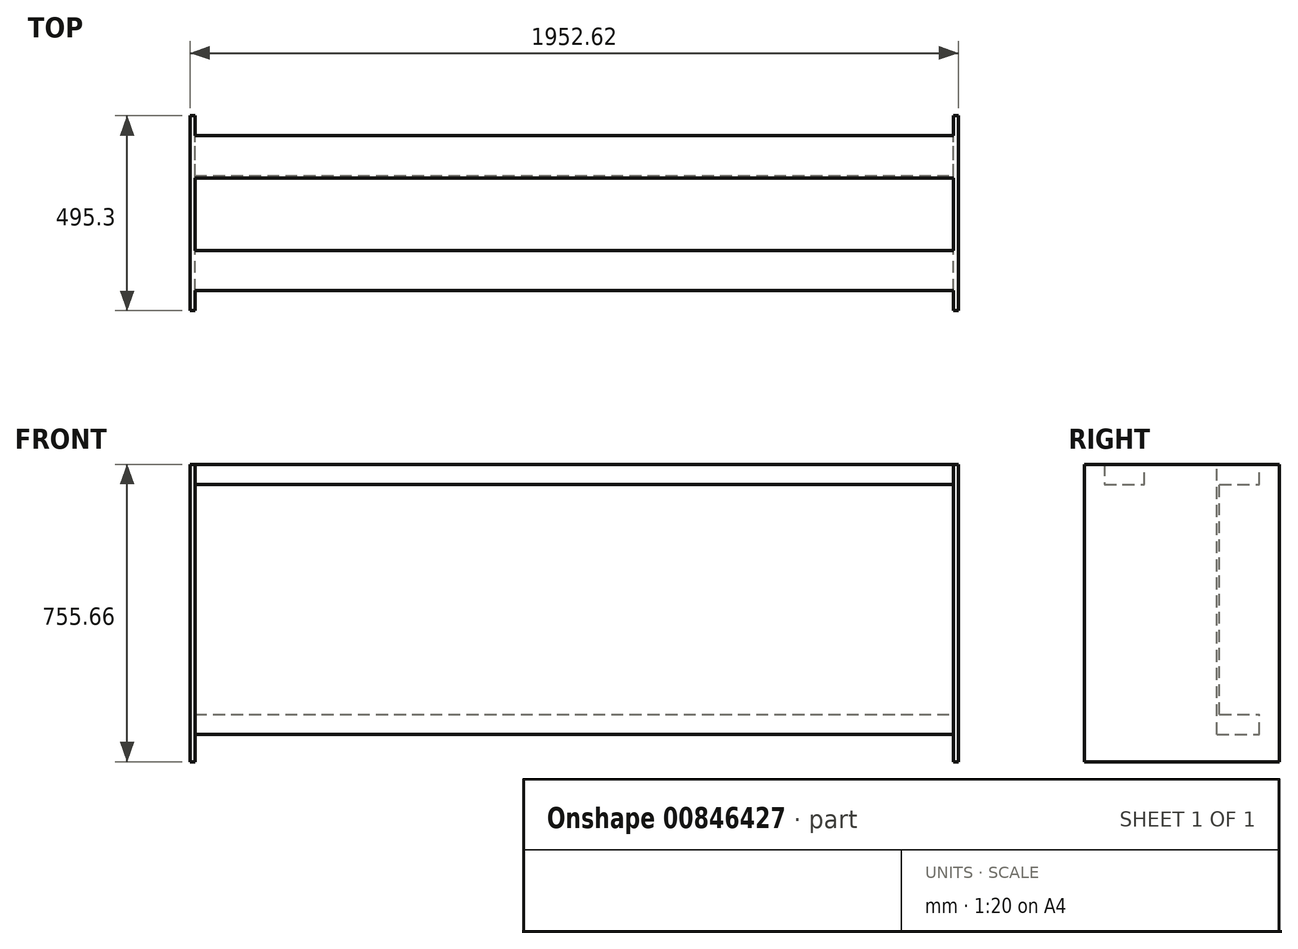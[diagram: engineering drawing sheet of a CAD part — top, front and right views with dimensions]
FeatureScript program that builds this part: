
annotation { "Feature Type Name" : "Feature", "Feature Type Description" : "" }
export const myFeature = defineFeature(function(context is Context, id is Id, definition is map)
    precondition{}
    {
        {
            var Q0;
            Q0=qCreatedBy(makeId("Front.planeOp"),FACE);
            var sketch = newSketch(context, id + "F0", { "sketchPlane" : qUnion([Q0])});
            skLineSegment(sketch, "E0.bottom", {"start": v(-976.31, -377.83) * mm, "end": v(976.31, -377.83) * mm});
            skLineSegment(sketch, "E0.top", {"start": v(-976.31, 377.83) * mm, "end": v(976.31, 377.83) * mm});
            skLineSegment(sketch, "E0.left", {"start": v(-976.31, -377.83) * mm, "end": v(-976.31, 377.83) * mm});
            skLineSegment(sketch, "E0.right", {"start": v(976.31, -377.83) * mm, "end": v(976.31, 377.83) * mm});
            skPoint(sketch, "E0.middle", {"position": v(0, 0) * mm});
            skLineSegment(sketch, "E1.0", {"start": v(-963.61, -377.83) * mm, "end": v(-963.61, 377.83) * mm});
            skLineSegment(sketch, "E2.0", {"start": v(963.61, -377.83) * mm, "end": v(963.61, 377.83) * mm});
            skLineSegment(sketch, "E3.0", {"start": v(-976.31, 327.03) * mm, "end": v(976.31, 327.03) * mm});
            skLineSegment(sketch, "E4.0", {"start": v(-976.31, -307.98) * mm, "end": v(976.31, -307.98) * mm});
            skLineSegment(sketch, "E5.0", {"start": v(-976.31, -257.18) * mm, "end": v(976.31, -257.18) * mm});
            skSolve(sketch);
        }
        {
            var Q0;
            {var subQ0=sQuery(id+"F0.wireOp",EDGE,"E0.left");var subQ1=sQuery(id+"F0.wireOp",EDGE,"E0.bottom");var subQ2=makeQuery(id+"F0.imprint","INTERSECT",VERTEX,{"derivedFrom":[subQ1,subQ0]});Q0=makeQuery(id+"F0.imprint","IMPRINT",FACE,{"disambiguationData":[TD([[makeQuery(id+"F0.imprint","IMPRINT",EDGE,{"disambiguationData":[TD([[subQ2,-1.0]])],"derivedFrom":subQ1}),1.0]])]});}
            var Q1;
            {var subQ0=sQuery(id+"F0.wireOp",EDGE,"E4.0");var subQ1=sQuery(id+"F0.wireOp",EDGE,"E0.left");var subQ2=makeQuery(id+"F0.imprint","INTERSECT",VERTEX,{"derivedFrom":[subQ1,subQ0]});Q1=makeQuery(id+"F0.imprint","IMPRINT",FACE,{"disambiguationData":[TD([[makeQuery(id+"F0.imprint","IMPRINT",EDGE,{"disambiguationData":[TD([[subQ2,-1.0]])],"derivedFrom":subQ1}),-1.0]])]});}
            var Q2;
            {var subQ0=sQuery(id+"F0.wireOp",EDGE,"E3.0");var subQ1=sQuery(id+"F0.wireOp",EDGE,"E0.left");var subQ2=makeQuery(id+"F0.imprint","INTERSECT",VERTEX,{"derivedFrom":[subQ1,subQ0]});Q2=makeQuery(id+"F0.imprint","IMPRINT",FACE,{"disambiguationData":[TD([[makeQuery(id+"F0.imprint","IMPRINT",EDGE,{"disambiguationData":[TD([[subQ2,1.0]])],"derivedFrom":subQ1}),-1.0]])]});}
            var Q3;
            {var subQ0=sQuery(id+"F0.wireOp",EDGE,"E0.left");var subQ1=sQuery(id+"F0.wireOp",EDGE,"E0.top");var subQ2=makeQuery(id+"F0.imprint","INTERSECT",VERTEX,{"derivedFrom":[subQ1,subQ0]});Q3=makeQuery(id+"F0.imprint","IMPRINT",FACE,{"disambiguationData":[TD([[makeQuery(id+"F0.imprint","IMPRINT",EDGE,{"disambiguationData":[TD([[subQ2,-1.0]])],"derivedFrom":subQ1}),-1.0]])]});}
            extrude(context, id + "F1", {"entities" : qUnion([Q0, Q1, Q2, Q3]), "depth" : 495.3 * mm, "offsetDistance" : 25.4 * mm});
        }
        {
            var Q0;
            {var subQ0=sQuery(id+"F0.wireOp",EDGE,"E1.0");var subQ1=sQuery(id+"F0.wireOp",EDGE,"E0.top");var subQ2=makeQuery(id+"F0.imprint","INTERSECT",VERTEX,{"derivedFrom":[subQ1,subQ0]});Q0=makeQuery(id+"F0.imprint","IMPRINT",FACE,{"disambiguationData":[TD([[makeQuery(id+"F0.imprint","IMPRINT",EDGE,{"disambiguationData":[TD([[subQ2,-1.0]])],"derivedFrom":subQ1}),-1.0]])]});}
            var Q1;
            {var subQ0=sQuery(id+"F0.wireOp",EDGE,"E4.0");var subQ1=sQuery(id+"F0.wireOp",EDGE,"E1.0");var subQ2=makeQuery(id+"F0.imprint","INTERSECT",VERTEX,{"derivedFrom":[subQ1,subQ0]});Q1=makeQuery(id+"F0.imprint","IMPRINT",FACE,{"disambiguationData":[TD([[makeQuery(id+"F0.imprint","IMPRINT",EDGE,{"disambiguationData":[TD([[subQ2,-1.0]])],"derivedFrom":subQ1}),-1.0]])]});}
            extrude(context, id + "F2", {"entities" : qUnion([Q0, Q1]), "operationType" : NewBodyOperationType.ADD, "depth" : 152.4 * mm, "offsetDistance" : 25.4 * mm});
        }
        {
            var Q0;
            {var subQ0=sQuery(id+"F0.wireOp",EDGE,"E5.0");var subQ1=sQuery(id+"F0.wireOp",EDGE,"E1.0");var subQ2=makeQuery(id+"F0.imprint","INTERSECT",VERTEX,{"derivedFrom":[subQ1,subQ0]});Q0=makeQuery(id+"F0.imprint","IMPRINT",FACE,{"disambiguationData":[TD([[makeQuery(id+"F0.imprint","IMPRINT",EDGE,{"disambiguationData":[TD([[subQ2,-1.0]])],"derivedFrom":subQ1}),-1.0]])]});}
            var Q1;
            {var subQ0=sQuery(id+"F0.wireOp",EDGE,"E1.0");var subQ1=sQuery(id+"F0.wireOp",EDGE,"E0.top");var subQ2=makeQuery(id+"F0.imprint","INTERSECT",VERTEX,{"derivedFrom":[subQ1,subQ0]});Q1=makeQuery(id+"F0.imprint","IMPRINT",FACE,{"disambiguationData":[TD([[makeQuery(id+"F0.imprint","IMPRINT",EDGE,{"disambiguationData":[TD([[subQ2,-1.0]])],"derivedFrom":subQ1}),-1.0]])]});}
            var Q2;
            {var subQ0=sQuery(id+"F0.wireOp",EDGE,"E4.0");var subQ1=sQuery(id+"F0.wireOp",EDGE,"E1.0");var subQ2=makeQuery(id+"F0.imprint","INTERSECT",VERTEX,{"derivedFrom":[subQ1,subQ0]});Q2=makeQuery(id+"F0.imprint","IMPRINT",FACE,{"disambiguationData":[TD([[makeQuery(id+"F0.imprint","IMPRINT",EDGE,{"disambiguationData":[TD([[subQ2,-1.0]])],"derivedFrom":subQ1}),-1.0]])]});}
            extrude(context, id + "F3", {"entities" : qUnion([Q0, Q1, Q2]), "operationType" : NewBodyOperationType.ADD, "depth" : 158.75 * mm, "offsetDistance" : 25.4 * mm});
        }
        {
            var Q0;
            {var subQ0=sQuery(id+"F0.wireOp",EDGE,"E3.0");var subQ1=sQuery(id+"F0.wireOp",EDGE,"E0.right");var subQ2=makeQuery(id+"F0.imprint","INTERSECT",VERTEX,{"derivedFrom":[subQ1,subQ0]});Q0=makeQuery(id+"F0.imprint","IMPRINT",FACE,{"disambiguationData":[TD([[makeQuery(id+"F0.imprint","IMPRINT",EDGE,{"disambiguationData":[TD([[subQ2,1.0]])],"derivedFrom":subQ1}),1.0]])]});}
            var Q1;
            {var subQ0=sQuery(id+"F0.wireOp",EDGE,"E0.right");var subQ1=sQuery(id+"F0.wireOp",EDGE,"E0.top");var subQ2=makeQuery(id+"F0.imprint","INTERSECT",VERTEX,{"derivedFrom":[subQ1,subQ0]});Q1=makeQuery(id+"F0.imprint","IMPRINT",FACE,{"disambiguationData":[TD([[makeQuery(id+"F0.imprint","IMPRINT",EDGE,{"disambiguationData":[TD([[subQ2,1.0]])],"derivedFrom":subQ1}),-1.0]])]});}
            var Q2;
            {var subQ0=sQuery(id+"F0.wireOp",EDGE,"E4.0");var subQ1=sQuery(id+"F0.wireOp",EDGE,"E0.right");var subQ2=makeQuery(id+"F0.imprint","INTERSECT",VERTEX,{"derivedFrom":[subQ1,subQ0]});Q2=makeQuery(id+"F0.imprint","IMPRINT",FACE,{"disambiguationData":[TD([[makeQuery(id+"F0.imprint","IMPRINT",EDGE,{"disambiguationData":[TD([[subQ2,-1.0]])],"derivedFrom":subQ1}),1.0]])]});}
            var Q3;
            {var subQ0=sQuery(id+"F0.wireOp",EDGE,"E0.right");var subQ1=sQuery(id+"F0.wireOp",EDGE,"E0.bottom");var subQ2=makeQuery(id+"F0.imprint","INTERSECT",VERTEX,{"derivedFrom":[subQ1,subQ0]});Q3=makeQuery(id+"F0.imprint","IMPRINT",FACE,{"disambiguationData":[TD([[makeQuery(id+"F0.imprint","IMPRINT",EDGE,{"disambiguationData":[TD([[subQ2,1.0]])],"derivedFrom":subQ1}),1.0]])]});}
            extrude(context, id + "F4", {"entities" : qUnion([Q0, Q1, Q2, Q3]), "operationType" : NewBodyOperationType.ADD, "depth" : 495.3 * mm, "offsetDistance" : 25.4 * mm});
        }
        {
            var Q0;
            {var subQ0=sQuery(id+"F0.wireOp",EDGE,"E1.0");var subQ1=sQuery(id+"F0.wireOp",EDGE,"E0.top");var subQ2=makeQuery(id+"F0.imprint","INTERSECT",VERTEX,{"derivedFrom":[subQ1,subQ0]});Q0=makeQuery(id+"F0.imprint","IMPRINT",FACE,{"disambiguationData":[TD([[makeQuery(id+"F0.imprint","IMPRINT",EDGE,{"disambiguationData":[TD([[subQ2,-1.0]])],"derivedFrom":subQ1}),-1.0]])]});}
            var Q1;
            {var subQ0=sQuery(id+"F0.wireOp",EDGE,"E4.0");var subQ1=sQuery(id+"F0.wireOp",EDGE,"E1.0");var subQ2=makeQuery(id+"F0.imprint","INTERSECT",VERTEX,{"derivedFrom":[subQ1,subQ0]});Q1=makeQuery(id+"F0.imprint","IMPRINT",FACE,{"disambiguationData":[TD([[makeQuery(id+"F0.imprint","IMPRINT",EDGE,{"disambiguationData":[TD([[subQ2,-1.0]])],"derivedFrom":subQ1}),-1.0]])]});}
            extrude(context, id + "F5", {"entities" : qUnion([Q0, Q1]), "operationType" : NewBodyOperationType.REMOVE, "depth" : 50.8 * mm, "offsetDistance" : 25.4 * mm});
        }
        {
            var Q0;
            Q0=makeQuery(id+"F1.opExtrude","SWEPT_FACE",FACE,{"disambiguationData":[OSD([sQuery(id+"F0.wireOp",EDGE,"E0.left")])]});
            var sketch = newSketch(context, id + "F6", { "sketchPlane" : qUnion([Q0])});
            skLineSegment(sketch, "E6", {"start": v(495.3, 377.83) * mm, "end": v(444.5, 377.83) * mm, "construction": true});
            skLineSegment(sketch, "E7", {"start": v(444.5, 377.83) * mm, "end": v(444.5, 327.03) * mm});
            skLineSegment(sketch, "E8", {"start": v(444.5, 327.03) * mm, "end": v(342.9, 327.03) * mm});
            skLineSegment(sketch, "E9", {"start": v(342.9, 327.03) * mm, "end": v(342.9, 377.83) * mm});
            skLineSegment(sketch, "E10", {"start": v(342.9, 377.83) * mm, "end": v(444.5, 377.83) * mm});
            skSolve(sketch);
        }
        {
            var Q0;
            Q0=makeQuery(id+"F6.imprint","IMPRINT",FACE,{"disambiguationData":[TD([[makeQuery(id+"F6.imprint","IMPRINT",EDGE,{"derivedFrom":sQuery(id+"F6.wireOp",EDGE,"E7")}),-1.0]])]});
            var Q1;
            Q1=makeQuery(id+"F4.opExtrude","SWEPT_FACE",FACE,{"disambiguationData":[OSD([sQuery(id+"F0.wireOp",EDGE,"E0.right")])]});
            extrude(context, id + "F7", {"entities" : qUnion([Q0]), "operationType" : NewBodyOperationType.ADD, "endBound" : BoundingType.UP_TO_SURFACE, "oppositeDirection" : true, "depth" : 25.4 * mm, "endBoundEntityFace" : qUnion([Q1]), "offsetDistance" : 25.4 * mm});
        }
        {
            var Q0;
            {var subQ0=sQuery(id+"F0.wireOp",EDGE,"E5.0");var subQ1=sQuery(id+"F0.wireOp",EDGE,"E1.0");var subQ2=makeQuery(id+"F0.imprint","INTERSECT",VERTEX,{"derivedFrom":[subQ1,subQ0]});Q0=makeQuery(id+"F0.imprint","IMPRINT",FACE,{"disambiguationData":[TD([[makeQuery(id+"F0.imprint","IMPRINT",EDGE,{"disambiguationData":[TD([[subQ2,-1.0]])],"derivedFrom":subQ1}),-1.0]])]});}
            extrude(context, id + "F8", {"entities" : qUnion([Q0]), "operationType" : NewBodyOperationType.REMOVE, "depth" : 152.4 * mm, "offsetDistance" : 25.4 * mm});
        }
    });
